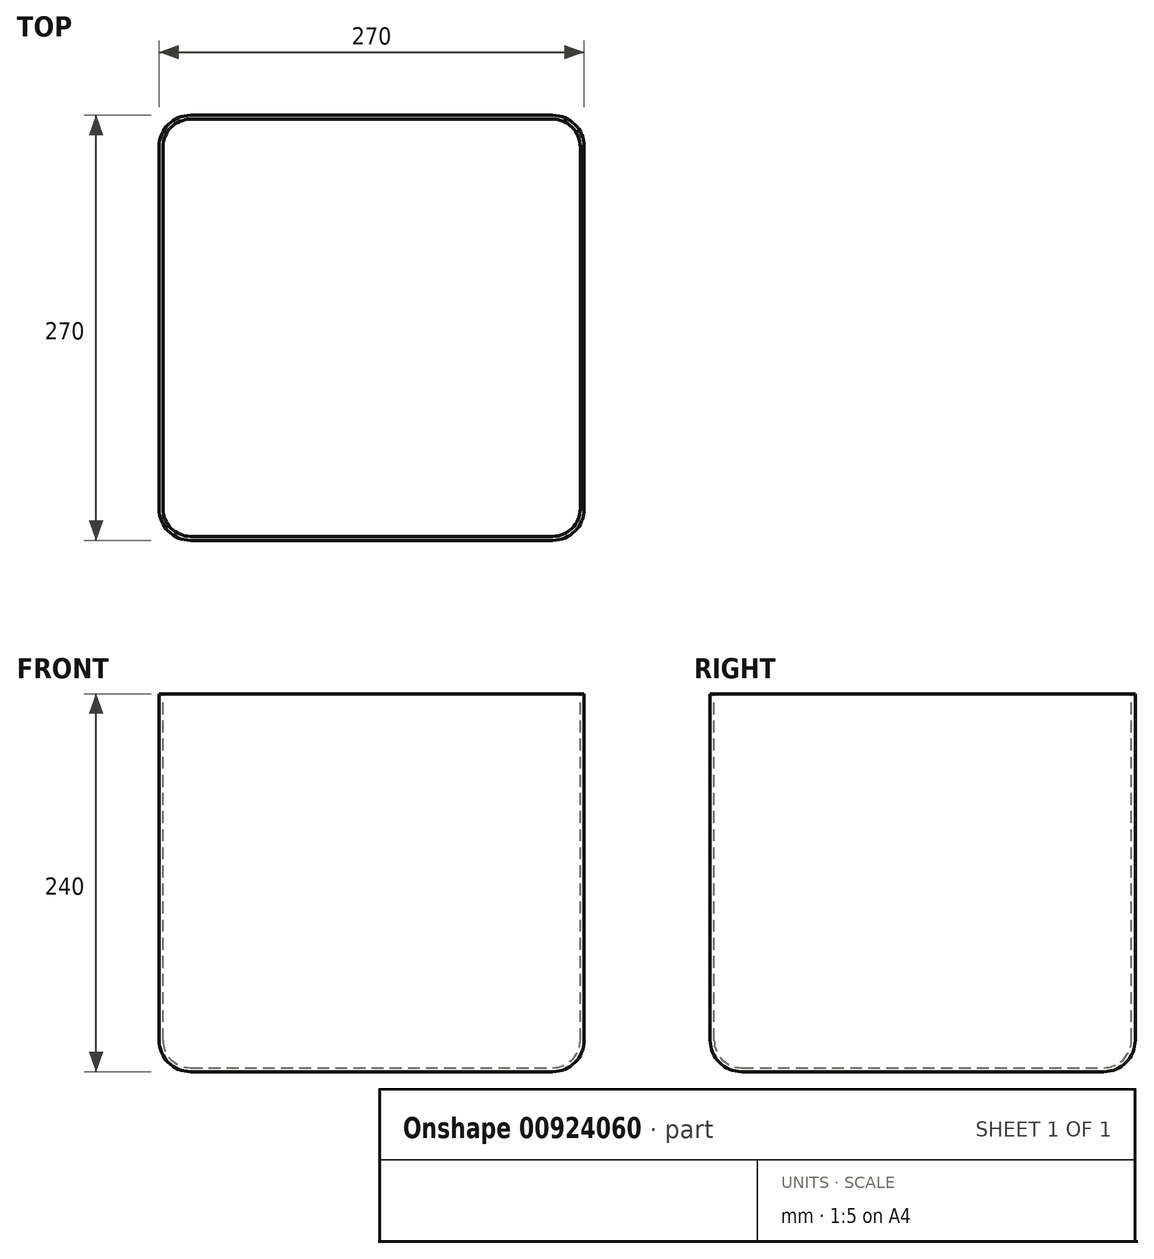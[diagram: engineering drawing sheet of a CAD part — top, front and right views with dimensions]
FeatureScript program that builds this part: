
annotation { "Feature Type Name" : "Feature", "Feature Type Description" : "" }
export const myFeature = defineFeature(function(context is Context, id is Id, definition is map)
    precondition{}
    {
        {
            var Q0;
            Q0=qCreatedBy(makeId("Top.planeOp"),FACE);
            var sketch = newSketch(context, id + "F0", { "sketchPlane" : qUnion([Q0])});
            skLineSegment(sketch, "E0.bottom", {"start": v(272.33, 135) * mm, "end": v(2.33, 135) * mm});
            skLineSegment(sketch, "E0.top", {"start": v(272.33, -135) * mm, "end": v(2.33, -135) * mm});
            skLineSegment(sketch, "E0.left", {"start": v(272.33, 135) * mm, "end": v(272.33, -135) * mm});
            skLineSegment(sketch, "E0.right", {"start": v(2.33, 135) * mm, "end": v(2.33, -135) * mm});
            skPoint(sketch, "E0.middle", {"position": v(137.33, 0) * mm});
            skSolve(sketch);
        }
        {
            var Q0;
            Q0 = qSketchRegion(id + "F0", true);
            extrude(context, id + "F1", {"entities" : qUnion([Q0]), "oppositeDirection" : true, "depth" : 240 * mm, "offsetDistance" : 25 * mm});
        }
        {
            var Q0;
            Q0=makeQuery(id+"F1.opExtrude","CAP_FACE",FACE,{"disambiguationData":[OSD([sQuery(id+"F0.wireOp",EDGE,"E0.bottom"),sQuery(id+"F0.wireOp",EDGE,"E0.top"),sQuery(id+"F0.wireOp",EDGE,"E0.left"),sQuery(id+"F0.wireOp",EDGE,"E0.right")])],"isStart":false});
            var Q1;
            Q1=makeQuery(id+"F1.opExtrude","SWEPT_EDGE",EDGE,{"disambiguationData":[OSD([sQuery(id+"F0.wireOp",EDGE,"E0.top"),sQuery(id+"F0.wireOp",EDGE,"E0.right")])]});
            var Q2;
            Q2=makeQuery(id+"F1.opExtrude","SWEPT_EDGE",EDGE,{"disambiguationData":[OSD([sQuery(id+"F0.wireOp",EDGE,"E0.top"),sQuery(id+"F0.wireOp",EDGE,"E0.left")])]});
            var Q3;
            Q3=makeQuery(id+"F1.opExtrude","SWEPT_EDGE",EDGE,{"disambiguationData":[OSD([sQuery(id+"F0.wireOp",EDGE,"E0.bottom"),sQuery(id+"F0.wireOp",EDGE,"E0.left")])]});
            var Q4;
            Q4=makeQuery(id+"F1.opExtrude","SWEPT_EDGE",EDGE,{"disambiguationData":[OSD([sQuery(id+"F0.wireOp",EDGE,"E0.bottom"),sQuery(id+"F0.wireOp",EDGE,"E0.right")])]});
            fillet(context, id + "F2", {"entities" : qUnion([Q0, Q1, Q2, Q3, Q4]), "radius" : 20 * mm, "tangentPropagation" : true, "allowEdgeOverflow" : false});
        }
        {
            var Q0;
            Q0=makeQuery(id+"F1.opExtrude","CAP_FACE",FACE,{"disambiguationData":[OSD([sQuery(id+"F0.wireOp",EDGE,"E0.bottom"),sQuery(id+"F0.wireOp",EDGE,"E0.top"),sQuery(id+"F0.wireOp",EDGE,"E0.left"),sQuery(id+"F0.wireOp",EDGE,"E0.right")])],"isStart":true});
            shell(context, id + "F3", {"entities" : qUnion([Q0]), "thickness" : 2.5 * mm});
        }
    });
